# Revit family: Deck_Plate-American_Standard-Selectronic-775P.x00_Series
name_source: partatom
category: Plumbing Fixtures
revit_build: Autodesk Revit 2014 (Build: 20130308_1515(x64)
units: mm (PartAtom-declared; Revit-internal decimal feet)

## types (2) — shared parameters
ADA Compliant = Yes
Actual Valve Water Flow = 0 GPM
Assembly Code = D2020300
CW Connection = Yes
CWFU = 1.5
Connection Diameter = 3/8"
Default Elevation = 0"
Description = Nextgen Selectronic Integrated Proximity Lavatory Faucet Battery Powered. Vandal-resistant multi-laminar spray.
HW Connection = Yes
HWFU = 1.5
Height = 5 3/4"
Installation Type = Deck Mounted
Length = 6 7/8"
Manufacturer = American Standard
Material = Metal-American Standard-002-Polished Chrome
Plate Width = 2 1/2"
Price = Prices may vary. Please consult Manufacturer Representative for most up-to-date price list.
Revised Date = 6/11/2014
URL = http://www.americanstandard-us.com
Vent Connection = No
Visible = Yes
Waste Connection = No
Width = 1 7/8"
zero-valued in all types: WFU

## per-type parameters (varying)
| type | Plate Length |
| 775P.400 | 4" |
| 775P.800 | 8" |

note: column(s) folded — value = type name in every type: Model

## geometry (parser evidence)
native form markers: Sweep x1
no freeform markers — native parametric forms only
